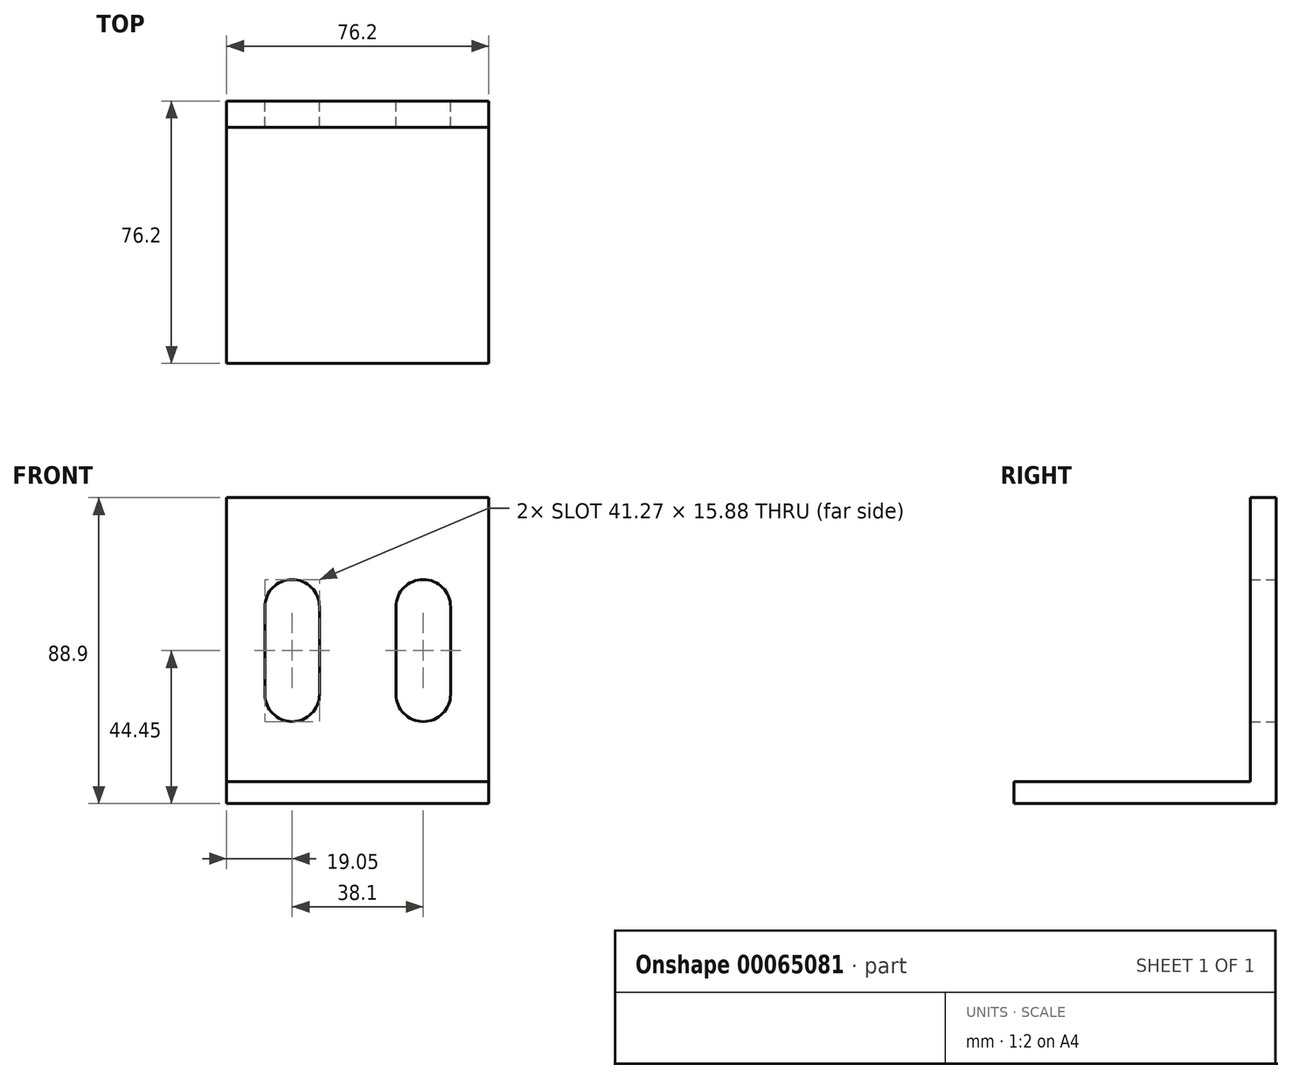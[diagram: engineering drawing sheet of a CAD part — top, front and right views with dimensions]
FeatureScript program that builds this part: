
annotation { "Feature Type Name" : "Feature", "Feature Type Description" : "" }
export const myFeature = defineFeature(function(context is Context, id is Id, definition is map)
    precondition{}
    {
        {
            var Q0;
            Q0=qCreatedBy(makeId("Front.planeOp"),FACE);
            var sketch = newSketch(context, id + "F0", { "sketchPlane" : qUnion([Q0])});
            skPoint(sketch, "E0.rect.middle", {"position": v(0, 0) * mm});
            skLineSegment(sketch, "E1", {"start": v(0, 44.57) * mm, "end": v(0, -52.28) * mm, "construction": true});
            skLineSegment(sketch, "E2", {"start": v(-19.05, 44.18) * mm, "end": v(-19.05, -53.26) * mm, "construction": true});
            skLineSegment(sketch, "E3", {"start": v(19.05, 44.2) * mm, "end": v(19.05, -52.28) * mm, "construction": true});
            skArc(sketch, "E4", {"start": v(-26.99, 12.7) * mm, "mid": v(-19.05, 20.64) * mm, "end": v(-11.11, 12.7) * mm});
            skLineSegment(sketch, "E5", {"start": v(-26.99, 12.7) * mm, "end": v(-26.99, 0) * mm});
            skLineSegment(sketch, "E6", {"start": v(-11.11, 12.7) * mm, "end": v(-11.11, 0) * mm});
            skLineSegment(sketch, "E7", {"start": v(-67.33, 0) * mm, "end": v(61.08, 0) * mm, "construction": true});
            skLineSegment(sketch, "E8.MirrorCS", {"start": v(-11.11, -12.7) * mm, "end": v(-11.11, 0) * mm});
            skLineSegment(sketch, "E9.MirrorCS", {"start": v(-26.99, -12.7) * mm, "end": v(-26.99, 0) * mm});
            skArc(sketch, "E10.MirrorCS", {"start": v(-26.99, -12.7) * mm, "mid": v(-19.05, -20.64) * mm, "end": v(-11.11, -12.7) * mm});
            skLineSegment(sketch, "E11.MirrorCS", {"start": v(0, -44.57) * mm, "end": v(0, 52.28) * mm, "construction": true});
            skLineSegment(sketch, "E12.MirrorCS", {"start": v(11.11, 12.7) * mm, "end": v(11.11, 0) * mm});
            skLineSegment(sketch, "E13.MirrorCS", {"start": v(11.11, -12.7) * mm, "end": v(11.11, 0) * mm});
            skArc(sketch, "E14.MirrorCS", {"start": v(26.99, -12.7) * mm, "mid": v(19.05, -20.64) * mm, "end": v(11.11, -12.7) * mm});
            skLineSegment(sketch, "E15.MirrorCS", {"start": v(26.99, -12.7) * mm, "end": v(26.99, 0) * mm});
            skLineSegment(sketch, "E16.MirrorCS", {"start": v(26.99, 12.7) * mm, "end": v(26.99, 0) * mm});
            skArc(sketch, "E17.MirrorCS", {"start": v(26.99, 12.7) * mm, "mid": v(19.05, 20.64) * mm, "end": v(11.11, 12.7) * mm});
            skLineSegment(sketch, "E18.rect.bottom", {"start": v(-38.1, 44.45) * mm, "end": v(38.1, 44.45) * mm});
            skLineSegment(sketch, "E18.rect.top", {"start": v(-38.1, -44.45) * mm, "end": v(38.1, -44.45) * mm});
            skLineSegment(sketch, "E18.rect.left", {"start": v(-38.1, 44.45) * mm, "end": v(-38.1, -44.45) * mm});
            skLineSegment(sketch, "E18.rect.right", {"start": v(38.1, 44.45) * mm, "end": v(38.1, -44.45) * mm});
            skLineSegment(sketch, "E19.top", {"start": v(-38.1, -38.1) * mm, "end": v(38.1, -38.1) * mm});
            skLineSegment(sketch, "E19.left", {"start": v(-38.1, -44.45) * mm, "end": v(-38.1, -38.1) * mm});
            skLineSegment(sketch, "E19.right", {"start": v(38.1, -44.45) * mm, "end": v(38.1, -38.1) * mm});
            skSolve(sketch);
        }
        {
            var Q0;
            Q0 = qSketchRegion(id + "F0", true);
            extrude(context, id + "F1", {"entities" : qUnion([Q0]), "depth" : 7.62 * mm});
        }
        {
            var Q0;
            Q0=makeQuery(id+"F0.imprint","IMPRINT",FACE,{"disambiguationData":[TD([[makeQuery(id+"F0.imprint","IMPRINT",EDGE,{"derivedFrom":sQuery(id+"F0.wireOp",EDGE,"E18.rect.top")}),1.0]])]});
            extrude(context, id + "F2", {"entities" : qUnion([Q0]), "operationType" : NewBodyOperationType.ADD, "depth" : 76.2 * mm});
        }
    });
